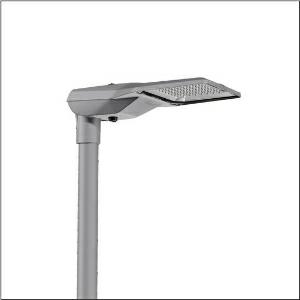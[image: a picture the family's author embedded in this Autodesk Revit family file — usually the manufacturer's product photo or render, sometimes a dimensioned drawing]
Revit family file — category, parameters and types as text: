
# Revit family: streetlight_sl_21_midi___st1_0a_5xe3d43t08mb_aa37
name_source: partatom
category: Lighting Fixtures
units: mm (PartAtom-declared; Revit-internal decimal feet)

## family parameters
Cut with Voids When Loaded = No
Host = Face
Light Source = No
Part Type = Normal
Room Calculation Point = No
Round Connector Dimension = Use Diameter
Shared = No

## types (1)
- --- (1 x LED, 20180 lm, 147 W, 4000K)
    Apparent Load = 147 VA
    CIE Flux Codes = 37 72 97 100 100
    Color Rendering = 70
    Color Temperature = 4000K
    Default Elevation = 1800 mm
    Description = Streetlight SL 21 midi, mast luminaire, primary light control with lens, of PMMA, primary optical cover: cover, of toughened safety glass, transparent, light distribution: ST1.0a, light emission: direct distribution, primary light characteristic: asymmetric, installation type: side-entry, post-top, LED, High Power LED, rated luminous flux: 20.180lm, luminous efficacy: 137lm/W, light colour: 740, colour temperature: 4000K, control gear: D4i, control: overheat protection, constant luminous flux control, time-dependent luminous flux control, flexible luminous flux parameterisation, pre-setting: logarithmic dimming characteristic, mains connection: 230..240V, AC, 50/60Hz, start of lifetime: 147W, end of service life: 155W, reduction: 65W, luminaire housing, of diecast aluminium, powder-coated, SITECO metallic grey (DB 702S), corrosivity category C5 high according to DIN EN ISO 12944, please order mast flange separately, inclination adjustable: 0°, 5°, 10°, 15°, sealing non-destructively replaceable, multi-level sealing system, length: 644mm, width: 335mm, height: 110mm, mast flange for spigot size: 42mm (side-entry): 5XC10008XM4, 60/48mm (side-entry/post-top): 5XC10108XM2, 76/60mm (side-entry/post-top): 5XC10108XM1, mounting height: 4..8m, Smart Interface below and above, protection rating (complete): IP66, insulation class (complete): insulation class II (safety insulation), certification: CE, ENEC, ENEC+, VDE, impact resistance: IK10, permissible operating ambient temperature for outdoor applications: -40..+50°C, standard-compliant lighting for roads and squares, packaging unit: 1 piece

Light Distribution: ST1.0a
    Height = 111 mm
    Lamp = 1 x LED
    Lamp Light Flux = 20180 lm
    Lamp Power = 147 W
    Lamp count = 1
    Length = 644 mm
    Luminous efficacy = 137 lm/W
    Manufacturer = Siteco
    ModVariant = No
    Model = 5XE3D43T08MB
    Number of Poles = 1
    OnlyDefault = Yes
    Power Factor = 1
    Product Name = Streetlight SL 21 midi | ST1.0a
    Product group = mast luminaire | pylon top
    ProductGroupID = 6100
    Protection Class = Protection class II
    Protection Degree = IP 66
    RLX_Detail_Level = 1
    RLX_Emergency_Light_Flux = 0 lm
    RLX_Emergency_Type = 0
    RLX_Emergency_Type_DB = No
    RlxData = <blob elided: 26961 chars, md5=9ec3b6a5>
    Socket = socket
    Standby Power = 0 W
    System Light Flux = 20180 lm
    System Power = 147 W
    Type Comments = factory setting: luminous flux: 100 % | dim-lin: 254 | 750 mA
    Type Image = l_1004304.jpg
    URL = http://relux.com
    VarID = @adj_186693
    Voltage = 0 V
    Weight = 0.00 kg
    Width = 336 mm

## geometry (parser evidence)
native form markers: Blend x4, Sweep x13
no freeform markers — native parametric forms only
